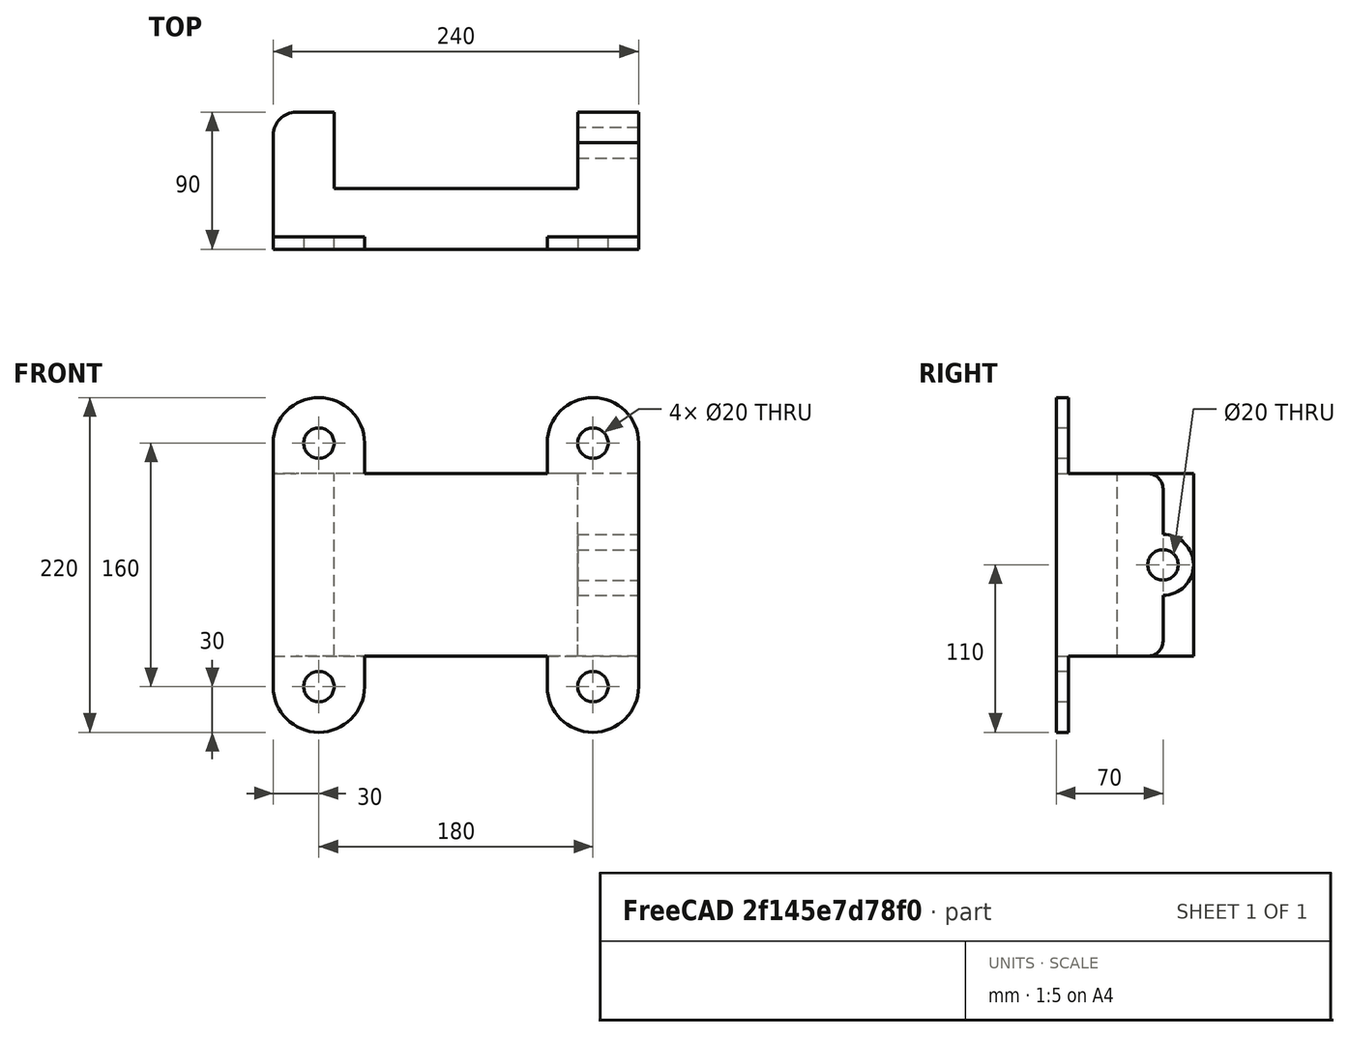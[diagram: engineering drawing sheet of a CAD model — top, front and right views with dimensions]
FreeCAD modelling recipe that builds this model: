
FCSTD DOCUMENT  (FreeCAD 0.18R4 (GitTag))
Label: Drawing 4 FreeCad Drawing for work bench 2nd sem
License: All rights reserved
LicenseURL: http://en.wikipedia.org/wiki/All_rights_reserved
objects: TechDraw::DrawViewDimension×15, Sketcher::SketchObject×9, TechDraw::DrawProjGroup×6, PartDesign::Pad×5, PartDesign::Pocket×4, TechDraw::DrawProjGroupItem×3, TechDraw::DrawViewAnnotation×3, PartDesign::Fillet×2, PartDesign::Body×1, TechDraw::DrawSVGTemplate×1, TechDraw::DrawPage×1
note: 30 computed .brp shape members not serialized (recipe doc carries the construction recipe); baked Part::Feature solids carry a one-line shape summary decoded from their .brp

FEATURE [Sketcher::SketchObject] Sketch
  MapMode = 5
  Support = -> [XY_Plane]
  sketch-geometry (8):
    g0: LineSegment StartX=-39.5 StartY=50 StartZ=0 EndX=-39.5 EndY=-40 EndZ=0
    g1: LineSegment StartX=-39.5 StartY=-40 StartZ=0 EndX=200.5 EndY=-40 EndZ=0
    g2: LineSegment StartX=200.5 StartY=-40 StartZ=0 EndX=200.5 EndY=30 EndZ=0
    g3: LineSegment StartX=200.5 StartY=30 StartZ=0 EndX=160.5 EndY=30 EndZ=0
    g4: LineSegment StartX=160.5 StartY=30 StartZ=0 EndX=160.5 EndY=0 EndZ=0
    g5: LineSegment StartX=160.5 StartY=0 StartZ=0 EndX=0.5 EndY=0 EndZ=0
    g6: LineSegment StartX=0.5 StartY=0 StartZ=0 EndX=0.5 EndY=50 EndZ=0
    g7: LineSegment StartX=0.5 StartY=50 StartZ=0 EndX=-39.5 EndY=50 EndZ=0
  constraints (23):
    c: Coincident(g0,g1)
    c: Coincident(g1,g2)
    c: Coincident(g2,g3)
    c: Coincident(g3,g4)
    c: Coincident(g4,g5)
    c: Coincident(g5,g6)
    c: Coincident(g6,g7)
    c: Coincident(g7,g0)
    c: Horizontal(g7)
    c: Horizontal(g3)
    c: Horizontal(g1)
    c: Horizontal(g5)
    c: Vertical(g6)
    c: Vertical(g0)
    c: Vertical(g4)
    c: Vertical(g2)
    c: DistanceX(g7,g7) = 40
    c: DistanceY(g0,g0) = 90
    c: DistanceY(g6,g6) = 50
    c: DistanceX(g5,g5) = 160
    c: DistanceX(g1,g1) = 240
    c: DistanceY(g2,g2) = 70
    c: Symmetric(g-1,g-1,g5)
FEATURE [PartDesign::Pad] Pad
  Length = 120
  Length2 = 100
  Profile = -> Sketch
  Type = 0
FEATURE [PartDesign::Fillet] Fillet
  Base = -> Pad [Edge1]
  BaseFeature = -> Pad
  Radius = 15
FEATURE [PartDesign::Fillet] Fillet001
  Base = -> Fillet [Edge20,Edge10]
  BaseFeature = -> Fillet
  Radius = 10
FEATURE [Sketcher::SketchObject] Sketch001
  ExternalGeometry = -> [Fillet001]
  MapMode = 5
  Placement = pos=(200.5,0,0) rot=(0.57735,0.57735,0.57735;2.0944rad)
  Support = -> [Fillet001]
  sketch-geometry (1):
    g0: Circle CenterX=30 CenterY=60 CenterZ=0 NormalX=0 NormalY=0 NormalZ=1 AngleXU=0 Radius=20
  constraints (3):
    c: PointOnObject(g0,g-3)
    c: DistanceY(g-1,g0) = 60
    c: Radius(g0) = 20
FEATURE [PartDesign::Pad] Pad001
  BaseFeature = -> Fillet001
  Length = 40
  Length2 = 100
  Profile = -> Sketch001
  Reversed = true
  Type = 0
FEATURE [Sketcher::SketchObject] Sketch002
  ExternalGeometry = -> [Pad001]
  MapMode = 5
  Placement = pos=(200.5,0,0) rot=(0.57735,0.57735,0.57735;2.0944rad)
  Support = -> [Pad001]
  sketch-geometry (1):
    g0: Circle CenterX=30 CenterY=60 CenterZ=0 NormalX=0 NormalY=0 NormalZ=1 AngleXU=0 Radius=10
  constraints (2):
    c: Coincident(g0,g-3)
    c: Radius(g0) = 10
FEATURE [PartDesign::Pocket] Pocket
  BaseFeature = -> Pad001
  Length = 40
  Length2 = 100
  Profile = -> Sketch002
  Type = 0
FEATURE [Sketcher::SketchObject] Sketch003
  ExternalGeometry = -> [Pocket]
  MapMode = 5
  Placement = pos=(0,-40,0) rot=(1,0,0;1.5708rad)
  Support = -> [Pocket]
  sketch-geometry (4):
    g0: LineSegment StartX=20.5 StartY=140 StartZ=0 EndX=20.5 EndY=120 EndZ=0
    g1: LineSegment StartX=20.5 StartY=120 StartZ=0 EndX=-39.5 EndY=120 EndZ=0
    g2: LineSegment StartX=-39.5 StartY=120 StartZ=0 EndX=-39.5 EndY=140 EndZ=0
    g3: ArcOfCircle CenterX=-9.5 CenterY=140 CenterZ=0 NormalX=0 NormalY=0 NormalZ=1 AngleXU=0 Radius=30 StartAngle=1.05365e-08 EndAngle=3.14159
  constraints (11):
    c: Coincident(g0,g1)
    c: Coincident(g1,g2)
    c: Horizontal(g1)
    c: Vertical(g0)
    c: Vertical(g2)
    c: Coincident(g1,g-3)
    c: DistanceX(g1,g1) = 60
    c: Coincident(g3,g0)
    c: Coincident(g3,g2)
    c: Radius(g3) = 30
    c: DistanceY(g2,g2) = 20
FEATURE [PartDesign::Pad] Pad002
  BaseFeature = -> Pocket
  Length = 8
  Length2 = 100
  Profile = -> Sketch003
  Reversed = true
  Type = 0
FEATURE [Sketcher::SketchObject] Sketch004
  ExternalGeometry = -> [Pad002]
  MapMode = 5
  Placement = pos=(0,-40,6e-15) rot=(1,0,0;1.5708rad)
  Support = -> [Pad002]
  sketch-geometry (1):
    g0: Circle CenterX=-9.5 CenterY=140 CenterZ=0 NormalX=0 NormalY=0 NormalZ=1 AngleXU=0 Radius=10
  constraints (2):
    c: Coincident(g0,g-3)
    c: Radius(g0) = 10
FEATURE [PartDesign::Pocket] Pocket001
  BaseFeature = -> Pad002
  Length = 8
  Length2 = 100
  Profile = -> Sketch004
  Type = 0
FEATURE [Sketcher::SketchObject] Sketch005
  ExternalGeometry = -> [Pocket001]
  MapMode = 5
  Placement = pos=(0,-40,0) rot=(1,0,0;1.5708rad)
  Support = -> [Pocket001]
  sketch-geometry (4):
    g0: LineSegment StartX=200.5 StartY=140 StartZ=0 EndX=200.5 EndY=120 EndZ=0
    g1: LineSegment StartX=200.5 StartY=120 StartZ=0 EndX=140.5 EndY=120 EndZ=0
    g2: LineSegment StartX=140.5 StartY=120 StartZ=0 EndX=140.5 EndY=140 EndZ=0
    g3: ArcOfCircle CenterX=170.5 CenterY=140 CenterZ=0 NormalX=0 NormalY=0 NormalZ=1 AngleXU=0 Radius=30 StartAngle=2.82107e-08 EndAngle=3.14159
  constraints (11):
    c: Coincident(g0,g1)
    c: Coincident(g1,g2)
    c: Horizontal(g1)
    c: Vertical(g0)
    c: Vertical(g2)
    c: Coincident(g0,g-3)
    c: DistanceX(g1,g1) = 60
    c: DistanceY(g0,g0) = 20
    c: Coincident(g3,g0)
    c: Coincident(g3,g2)
    c: Radius(g3) = 30
FEATURE [PartDesign::Pad] Pad003
  BaseFeature = -> Pocket001
  Length = 8
  Length2 = 100
  Profile = -> Sketch005
  Reversed = true
  Type = 0
FEATURE [Sketcher::SketchObject] Sketch006
  ExternalGeometry = -> [Pad003]
  MapMode = 5
  Placement = pos=(0,-40,6e-15) rot=(1,0,0;1.5708rad)
  Support = -> [Pad003]
  sketch-geometry (1):
    g0: Circle CenterX=170.5 CenterY=140 CenterZ=0 NormalX=0 NormalY=0 NormalZ=1 AngleXU=0 Radius=10
  constraints (2):
    c: Coincident(g-3,g0)
    c: Radius(g0) = 10
FEATURE [PartDesign::Pocket] Pocket002
  BaseFeature = -> Pad003
  Length = 8
  Length2 = 100
  Profile = -> Sketch006
  Type = 0
FEATURE [Sketcher::SketchObject] Sketch007
  ExternalGeometry = -> [Pocket002]
  MapMode = 5
  Placement = pos=(0,-40,0) rot=(1,0,0;1.5708rad)
  Support = -> [Pocket002]
  sketch-geometry (8):
    g0: LineSegment StartX=-39.5 StartY=0 StartZ=0 EndX=20.5 EndY=0 EndZ=0
    g1: LineSegment StartX=20.5 StartY=0 StartZ=0 EndX=20.5 EndY=-20 EndZ=0
    g2: LineSegment StartX=-39.5 StartY=-20 StartZ=0 EndX=-39.5 EndY=0 EndZ=0
    g3: LineSegment StartX=140.5 StartY=0 StartZ=0 EndX=200.5 EndY=0 EndZ=0
    g4: LineSegment StartX=200.5 StartY=0 StartZ=0 EndX=200.5 EndY=-20 EndZ=0
    g5: LineSegment StartX=140.5 StartY=-20 StartZ=0 EndX=140.5 EndY=0 EndZ=0
    g6: ArcOfCircle CenterX=170.5 CenterY=-20 CenterZ=0 NormalX=0 NormalY=0 NormalZ=1 AngleXU=0 Radius=30 StartAngle=3.14159 EndAngle=6.28318
    g7: ArcOfCircle CenterX=-9.5 CenterY=-20 CenterZ=0 NormalX=0 NormalY=0 NormalZ=1 AngleXU=0 Radius=30 StartAngle=3.14159 EndAngle=6.28319
  constraints (24):
    c: Coincident(g0,g1)
    c: Coincident(g2,g0)
    c: Horizontal(g0)
    c: Vertical(g1)
    c: Vertical(g2)
    c: Coincident(g3,g4)
    c: Coincident(g5,g3)
    c: Horizontal(g3)
    c: Vertical(g4)
    c: Vertical(g5)
    c: Coincident(g3,g-4)
    c: Coincident(g0,g-3)
    c: DistanceX(g0,g0) = 60
    c: DistanceY(g2,g2) = 20
    c: DistanceX(g3,g3) = 60
    c: DistanceY(g5,g5) = 20
    c: Coincident(g6,g5)
    c: Coincident(g6,g4)
    c: Coincident(g7,g2)
    c: Coincident(g7,g1)
    c: DistanceY(g1,g1) = 20
    c: Radius(g7) = 30
    c: DistanceY(g4,g4) = 20
    c: Radius(g6) = 30
FEATURE [PartDesign::Pad] Pad004
  BaseFeature = -> Pocket002
  Length = 8
  Length2 = 100
  Profile = -> Sketch007
  Reversed = true
  Type = 0
FEATURE [Sketcher::SketchObject] Sketch008
  ExternalGeometry = -> [Pad004]
  MapMode = 5
  Placement = pos=(0,-40,0) rot=(1,0,0;1.5708rad)
  Support = -> [Pad004]
  sketch-geometry (2):
    g0: Circle CenterX=-9.5 CenterY=-20 CenterZ=0 NormalX=0 NormalY=0 NormalZ=1 AngleXU=0 Radius=10
    g1: Circle CenterX=170.5 CenterY=-20 CenterZ=0 NormalX=0 NormalY=0 NormalZ=1 AngleXU=0 Radius=10
  constraints (4):
    c: Coincident(g1,g-4)
    c: Radius(g1) = 10
    c: Coincident(g0,g-3)
    c: Radius(g0) = 10
FEATURE [PartDesign::Pocket] Pocket003
  BaseFeature = -> Pad004
  Length = 8
  Length2 = 100
  Profile = -> Sketch008
  Type = 0
FEATURE [PartDesign::Body] Body
  Group = -> [Sketch,Pad,Fillet,Fillet001,Sketch001,Pad001,Sketch002,Pocket,Sketch003,Pad002,Sketch004,Pocket001,Sketch005,Pad003,Sketch006,Pocket002,Sketch007,Pad004,Sketch008,Pocket003]
  Origin = -> Origin
  Tip = -> Pocket003
FEATURE [TechDraw::DrawSVGTemplate] Template
  EditableTexts = Designed_by_Name=Soumojit Shome; Drawing_number=Drawing number-3; FC-Date=09/05/2023; FC-SC=1:2; FC-SH=03; FC-Title=Academy of Technology; Subtitle=16900322101 ECE2(Y); Weight=Weight
  Height = 210
  Orientation = 1
  Width = 297
FEATURE [TechDraw::DrawProjGroup] ProjGroup
  AutoDistribute = true
  LockPosition = false
  ProjectionType = 0
  Rotation = 0
  Scale = 0.5
  ScaleType = 2
  Source = -> [Pocket003]
  X = 79.6067
  Y = 72.6285
  spacingX = 15
  spacingY = 15
FEATURE [TechDraw::DrawProjGroup] ProjGroup001
  AutoDistribute = true
  LockPosition = false
  ProjectionType = 0
  Rotation = 0
  Scale = 0.5
  ScaleType = 2
  Source = -> [Pocket003]
  X = 84.1719
  Y = 168.083
  spacingX = 15
  spacingY = 15
FEATURE [TechDraw::DrawProjGroup] ProjGroup002
  AutoDistribute = true
  LockPosition = false
  ProjectionType = 0
  Rotation = 0
  Scale = 0.5
  ScaleType = 2
  Source = -> [Pocket003]
  X = 209.923
  Y = 134.881
  spacingX = 15
  spacingY = 15
FEATURE [TechDraw::DrawProjGroupItem] ProjItem  label="Front"
  CoarseView = false
  Direction = (0,1,0)
  Focus = 100
  HardHidden = false
  IsoCount = 0
  IsoHidden = false
  IsoVisible = false
  LockPosition = true
  Perspective = false
  Rotation = 0
  RotationVector = (0,0,-1)
  Scale = 0.333333
  ScaleType = 2
  SeamHidden = false
  SeamVisible = false
  SmoothHidden = false
  SmoothVisible = false
  Source = -> [Pocket003]
  Type = 0
  X = 0
  Y = 0
FEATURE [TechDraw::DrawProjGroup] ProjGroup003
  Anchor = -> ProjItem
  AutoDistribute = true
  LockPosition = false
  ProjectionType = 1
  Rotation = 0
  Scale = 0.333333
  ScaleType = 2
  Source = -> [Pocket003]
  Views = -> [ProjItem]
  X = 77.5316
  Y = 70.3827
  spacingX = 15
  spacingY = 15
FEATURE [TechDraw::DrawProjGroupItem] ProjItem001  label="Front001"
  CoarseView = false
  Direction = (1,0,0)
  Focus = 100
  HardHidden = false
  IsoCount = 0
  IsoHidden = false
  IsoVisible = false
  LockPosition = true
  Perspective = false
  Rotation = 0
  RotationVector = (0,0,-1)
  Scale = 0.333333
  ScaleType = 2
  SeamHidden = false
  SeamVisible = false
  SmoothHidden = false
  SmoothVisible = false
  Source = -> [Pocket003]
  Type = 0
  X = 0
  Y = 0
FEATURE [TechDraw::DrawProjGroup] ProjGroup004
  Anchor = -> ProjItem001
  AutoDistribute = true
  LockPosition = false
  ProjectionType = 0
  Rotation = 0
  Scale = 0.333333
  ScaleType = 2
  Source = -> [Pocket003]
  Views = -> [ProjItem001]
  X = 75.0415
  Y = 168.448
  spacingX = 15
  spacingY = 15
FEATURE [TechDraw::DrawProjGroupItem] ProjItem002  label="Front002"
  CoarseView = false
  Direction = (0.631,0.499,0.594)
  Focus = 100
  HardHidden = false
  IsoCount = 0
  IsoHidden = false
  IsoVisible = false
  LockPosition = true
  Perspective = false
  Rotation = 0
  RotationVector = (0.668,0.04,-0.743)
  Scale = 0.333333
  ScaleType = 2
  SeamHidden = false
  SeamVisible = false
  SmoothHidden = false
  SmoothVisible = false
  Source = -> [Pocket003]
  Type = 0
  X = 0
  Y = 0
FEATURE [TechDraw::DrawProjGroup] ProjGroup005
  Anchor = -> ProjItem002
  AutoDistribute = true
  LockPosition = false
  ProjectionType = 0
  Rotation = 0
  Scale = 0.333333
  ScaleType = 2
  Source = -> [Pocket003]
  Views = -> [ProjItem002]
  X = 208.11
  Y = 133.926
  spacingX = 15
  spacingY = 15
FEATURE [TechDraw::DrawViewAnnotation] Annotation
  Font = osifont
  LineSpace = 80
  LockPosition = false
  MaxWidth = -1
  Rotation = 0
  ScaleType = 0
  Text = Isometric View
  TextSize = 6
  TextStyle = 0
  X = 215.172
  Y = 86.2639
FEATURE [TechDraw::DrawViewAnnotation] Annotation001
  Font = osifont
  LineSpace = 80
  LockPosition = false
  MaxWidth = -1
  Rotation = 0
  ScaleType = 0
  Text = Top View
  TextSize = 6
  TextStyle = 0
  X = 77.4211
  Y = 20.2221
FEATURE [TechDraw::DrawViewAnnotation] Annotation002
  Font = osifont
  LineSpace = 80
  LockPosition = false
  MaxWidth = -1
  Rotation = 0
  ScaleType = 0
  Text = Front View 
  TextSize = 6
  TextStyle = 0
  X = 76.1092
  Y = 134.657
FEATURE [TechDraw::DrawViewDimension] Dimension
  Arbitrary = false
  FormatSpec = R%.2f
  LockPosition = false
  MeasureType = 1
  OverTolerance = 0
  References2D = -> [ProjItem001]
  Rotation = 0
  ScaleType = 0
  Type = 4
  UnderTolerance = 0
  X = 44.4373
  Y = 23.288
FEATURE [TechDraw::DrawViewDimension] Dimension001
  Arbitrary = false
  FormatSpec = ⌀%.2f
  LockPosition = false
  MeasureType = 1
  OverTolerance = 0
  References2D = -> [ProjItem001]
  Rotation = 0
  ScaleType = 0
  Type = 5
  UnderTolerance = 0
  X = -37.546
  Y = 27.0901
FEATURE [TechDraw::DrawViewDimension] Dimension002
  Arbitrary = false
  FormatSpec = R%.2f
  LockPosition = false
  MeasureType = 1
  OverTolerance = 0
  References2D = -> [ProjItem001]
  Rotation = 0
  ScaleType = 0
  Type = 4
  UnderTolerance = 0
  X = -48.2394
  Y = 17.5848
FEATURE [TechDraw::DrawViewDimension] Dimension003
  Arbitrary = false
  FormatSpec = %.2f
  LockPosition = false
  MeasureType = 1
  OverTolerance = 0
  References2D = -> [ProjItem001]
  Rotation = 0
  ScaleType = 0
  Type = 1
  UnderTolerance = 0
  X = 0.237633
  Y = -24.5053
FEATURE [TechDraw::DrawViewDimension] Dimension004
  Arbitrary = false
  FormatSpec = %.2f
  LockPosition = false
  MeasureType = 1
  OverTolerance = 0
  References2D = -> [ProjItem001]
  Rotation = 0
  ScaleType = 0
  Type = 1
  UnderTolerance = 0
  X = 14.7591
  Y = 29.6084
FEATURE [TechDraw::DrawViewDimension] Dimension005
  Arbitrary = false
  FormatSpec = %.2f
  LockPosition = false
  MeasureType = 1
  OverTolerance = 0
  References2D = -> [ProjItem001]
  Rotation = 0
  ScaleType = 0
  Type = 1
  UnderTolerance = 0
  X = -31.1752
  Y = -3.77855
FEATURE [TechDraw::DrawViewDimension] Dimension006
  Arbitrary = false
  FormatSpec = %.2f
  LockPosition = false
  MeasureType = 1
  OverTolerance = 0
  References2D = -> [ProjItem]
  Rotation = 0
  ScaleType = 0
  Type = 1
  UnderTolerance = 0
  X = 0
  Y = 47.1289
FEATURE [TechDraw::DrawViewDimension] Dimension007
  Arbitrary = false
  FormatSpec = %.2f
  LockPosition = false
  MeasureType = 1
  OverTolerance = 0
  References2D = -> [ProjItem]
  Rotation = 0
  ScaleType = 0
  Type = 2
  UnderTolerance = 0
  X = -50.1793
  Y = -29.0559
FEATURE [TechDraw::DrawViewDimension] Dimension008
  Arbitrary = false
  FormatSpec = R%.2f
  LockPosition = false
  MeasureType = 1
  OverTolerance = 0
  References2D = -> [ProjItem]
  Rotation = 0
  ScaleType = 0
  Type = 4
  UnderTolerance = 0
  X = -56.3189
  Y = -1.66343
FEATURE [TechDraw::DrawViewDimension] Dimension009
  Arbitrary = false
  FormatSpec = ⌀%.2f
  LockPosition = false
  MeasureType = 1
  OverTolerance = 0
  References2D = -> [ProjItem]
  Rotation = 0
  ScaleType = 0
  Type = 5
  UnderTolerance = 0
  X = -50.3781
  Y = 48.9523
FEATURE [TechDraw::DrawViewDimension] Dimension010
  Arbitrary = false
  FormatSpec = %.2f
  LockPosition = false
  MeasureType = 1
  OverTolerance = 0
  References2D = -> [ProjItem]
  Rotation = 0
  ScaleType = 0
  Type = 2
  UnderTolerance = 0
  X = -50.1793
  Y = 37.3731
FEATURE [TechDraw::DrawViewDimension] Dimension011
  Arbitrary = false
  FormatSpec = %.2f
  LockPosition = false
  MeasureType = 1
  OverTolerance = 0
  References2D = -> [ProjItem]
  Rotation = 0
  ScaleType = 0
  Type = 2
  UnderTolerance = 0
  X = 46.3901
  Y = 0.950531
FEATURE [TechDraw::DrawViewDimension] Dimension012
  Arbitrary = false
  FormatSpec = %.2f
  LockPosition = false
  MeasureType = 1
  OverTolerance = 0
  References2D = -> [ProjItem001]
  Rotation = 0
  ScaleType = 0
  Type = 2
  UnderTolerance = 0
  X = 46.6472
  Y = -14.3796
FEATURE [TechDraw::DrawViewDimension] Dimension013
  Arbitrary = false
  FormatSpec = %.2f
  LockPosition = false
  MeasureType = 1
  OverTolerance = 0
  References2D = -> [ProjItem001]
  Rotation = 0
  ScaleType = 0
  Type = 2
  UnderTolerance = 0
  X = -55.0239
  Y = -3.32991
FEATURE [TechDraw::DrawViewDimension] Dimension014
  Arbitrary = false
  FormatSpec = %.2f
  LockPosition = false
  MeasureType = 1
  OverTolerance = 0
  References2D = -> [ProjItem001]
  Rotation = 0
  ScaleType = 0
  Type = 2
  UnderTolerance = 0
  X = 59.1934
  Y = -2.50171
FEATURE [TechDraw::DrawPage] Page
  KeepUpdated = true
  ProjectionType = 0
  Template = -> Template
  Views = -> [ProjGroup,ProjGroup001,ProjGroup002,ProjGroup003,ProjGroup004,ProjGroup005,Annotation,Annotation001,Annotation002,Dimension,Dimension001,Dimension002,Dimension003,Dimension004,Dimension005,Dimension006,Dimension007,Dimension008,Dimension009,Dimension010,Dimension011,Dimension012,Dimension013,Dimension014]
